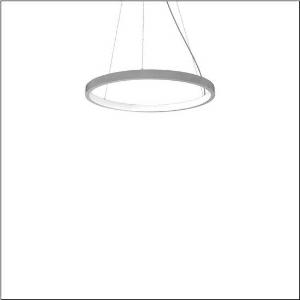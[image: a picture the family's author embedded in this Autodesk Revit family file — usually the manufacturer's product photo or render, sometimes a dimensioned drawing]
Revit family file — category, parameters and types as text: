
# Revit family: silica_21_ring-i_5pjbi2d1204a
name_source: partatom
category: Lighting Fixtures
units: mm (PartAtom-declared; Revit-internal decimal feet)

## family parameters
Cut with Voids When Loaded = No
Host = Face
Light Source = No
Part Type = Normal
Room Calculation Point = No
Round Connector Dimension = Use Diameter
Shared = No

## types (1)
- Silica 21 Ring-I (1 x LED, 4800 lm, 80 W, 3000K)
    Apparent Load = 80 VA
    CIE Flux Codes = 22 48 76 50 101
    Color Rendering = 80
    Color Temperature = 3000K
    Default Elevation = 1800 mm
    Description = Silica 21 Ring-I, suspended luminaire, of PMMA, frosted, light emission: inner ring side luminous distribution, primary light characteristic: symmetric, installation type: suspended mounting, LED, rated luminous flux: 4.800lm, luminous efficacy: 60lm/W, light colour: 830, colour temperature: 3000K, control gear: DALI 2, with terminal, 5-pole, mains connection: 230V, AC/DC, 0/50..60Hz, rated input power: 80W, housing, of extruded aluminium section, metallic grey (RAL 9006), diameter: 805mm, ceiling canopy, metallic grey (RAL 9006), protection rating (lamp compartment): IP40, insulation class (complete): insulation class I (protective earthing), certification: CE, impact resistance: IK02, permissible operating ambient temperature: 0..+35°C, packaging unit: 1 piece
    Height = 48 mm  [stored 0.15748 ft]
    Lamp = 1 x LED
    Lamp Light Flux = 4800 lm
    Lamp Power = 80 W
    Lamp count = 1
    Length = 805 mm
    Luminous efficacy = 60 lm/W
    Manufacturer = Siteco
    ModVariant = No
    Model = 5PJBI2D1204A
    Mounting Place = Ceiling
    Mounting Type = Pendant
    Number of Poles = 1
    OnlyDefault = Yes
    Power Factor = 1
    Product Name = Silica 21 Ring-I
    Product group = suspended luminaire
    ProductGroupID = 904
    Protection Class = Protection class I
    Protection Degree = IP 40
    RLX_Detail_Level = 1
    RLX_Emergency_Light_Flux = 0 lm
    RLX_Emergency_Type = 0
    RLX_Emergency_Type_DB = No
    RlxData = <blob elided: 13093 chars, md5=a86b45bc>
    Socket = socket
    Standby Power = 0 W
    System Light Flux = 4800 lm
    System Power = 80 W
    Type Comments = Product without accessories
    Type Image = l_1251752.jpg
    URL = http://relux.com
    VarID = ---
    Voltage = 0 V
    Weight = 0.00 kg
    Width = 0 mm  [stored 0 ft]

note: [stored X ft] marks values corroborated as IEEE doubles in the binary element streams (Revit-internal decimal feet)

## geometry (parser evidence)
native form markers: Sweep x9
no freeform markers — native parametric forms only
